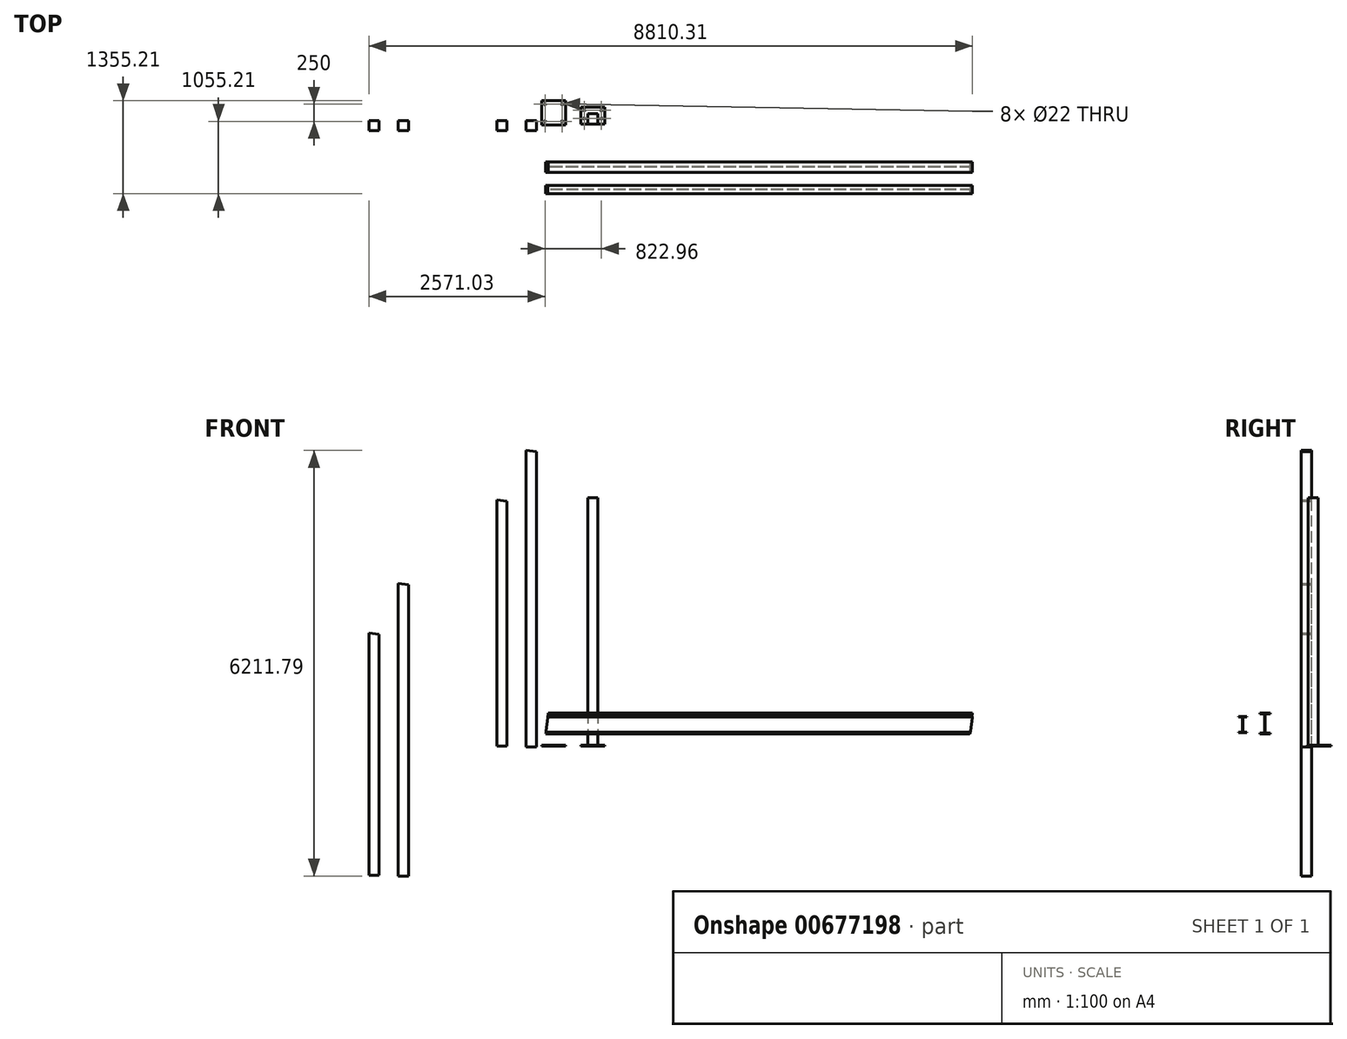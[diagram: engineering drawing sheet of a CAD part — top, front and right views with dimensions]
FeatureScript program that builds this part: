
annotation { "Feature Type Name" : "Feature", "Feature Type Description" : "" }
export const myFeature = defineFeature(function(context is Context, id is Id, definition is map)
    precondition{}
    {
        {
            var Q0;
            Q0=qCreatedBy(makeId("Top.planeOp"),FACE);
            var sketch = newSketch(context, id + "F0", { "sketchPlane" : qUnion([Q0])});
            skLineSegment(sketch, "E0.bottom", {"start": v(-62.2, -61.8) * mm, "end": v(287.8, -61.8) * mm});
            skLineSegment(sketch, "E0.top", {"start": v(-62.2, 288.2) * mm, "end": v(287.8, 288.2) * mm});
            skLineSegment(sketch, "E0.left", {"start": v(-62.2, -61.8) * mm, "end": v(-62.2, 288.2) * mm});
            skLineSegment(sketch, "E0.right", {"start": v(287.8, -61.8) * mm, "end": v(287.8, 288.2) * mm});
            skCircle(sketch, "E1", {"center": v(-12.2, -11.8) * mm, "radius": 11 * mm});
            skCircle(sketch, "E2", {"center": v(-12.2, 238.2) * mm, "radius": 11 * mm});
            skCircle(sketch, "E3", {"center": v(237.8, 238.2) * mm, "radius": 11 * mm});
            skCircle(sketch, "E4", {"center": v(237.8, -11.8) * mm, "radius": 11 * mm});
            skLineSegment(sketch, "E5.bottom", {"start": v(510.77, -51.32) * mm, "end": v(860.77, -51.32) * mm});
            skLineSegment(sketch, "E5.top", {"start": v(510.77, 198.68) * mm, "end": v(860.77, 198.68) * mm});
            skLineSegment(sketch, "E5.left", {"start": v(510.77, -51.32) * mm, "end": v(510.77, 198.68) * mm});
            skLineSegment(sketch, "E5.right", {"start": v(860.77, -51.32) * mm, "end": v(860.77, 198.68) * mm});
            skCircle(sketch, "E6", {"center": v(560.77, 148.68) * mm, "radius": 11 * mm});
            skCircle(sketch, "E7", {"center": v(560.77, 28.68) * mm, "radius": 11 * mm});
            skCircle(sketch, "E8", {"center": v(810.77, 148.68) * mm, "radius": 11 * mm});
            skCircle(sketch, "E9", {"center": v(810.77, 28.68) * mm, "radius": 11 * mm});
            skSolve(sketch);
        }
        {
            var Q0;
            Q0=makeQuery(id+"F0.imprint","IMPRINT",FACE,{"disambiguationData":[TD([[makeQuery(id+"F0.imprint","IMPRINT",EDGE,{"derivedFrom":sQuery(id+"F0.wireOp",EDGE,"E0.bottom")}),1.0]])]});
            var Q1;
            Q1=makeQuery(id+"F0.imprint","IMPRINT",FACE,{"disambiguationData":[TD([[makeQuery(id+"F0.imprint","IMPRINT",EDGE,{"derivedFrom":sQuery(id+"F0.wireOp",EDGE,"E5.bottom")}),1.0]])]});
            extrude(context, id + "F1", {"entities" : qUnion([Q0, Q1]), "depth" : 12 * mm, "offsetDistance" : 25 * mm});
        }
        {
            var Q0;
            Q0=qCreatedBy(makeId("Front.planeOp"),FACE);
            var sketch = newSketch(context, id + "F2", { "sketchPlane" : qUnion([Q0])});
            skLineSegment(sketch, "E10", {"start": v(-288.06, -13.37) * mm, "end": v(-288.06, 4317.72) * mm});
            skLineSegment(sketch, "E11", {"start": v(-288.06, -13.37) * mm, "end": v(-138.06, -13.37) * mm});
            skLineSegment(sketch, "E12", {"start": v(-138.06, -13.37) * mm, "end": v(-138.06, 4299.3) * mm});
            skLineSegment(sketch, "E13", {"start": v(-138.06, 4299.3) * mm, "end": v(-288.06, 4317.72) * mm});
            skLineSegment(sketch, "E14", {"start": v(-715.76, 0) * mm, "end": v(-715.76, 3594.5) * mm});
            skLineSegment(sketch, "E15", {"start": v(-715.76, 0) * mm, "end": v(-565.76, 0) * mm});
            skLineSegment(sketch, "E16", {"start": v(-565.76, 0) * mm, "end": v(-565.76, 3576.09) * mm});
            skLineSegment(sketch, "E17", {"start": v(-565.76, 3576.09) * mm, "end": v(-715.76, 3594.5) * mm});
            skLineSegment(sketch, "E18", {"start": v(-2155.53, -1954.07) * mm, "end": v(-2155.53, 2377.02) * mm});
            skLineSegment(sketch, "E19", {"start": v(-2155.53, -1954.07) * mm, "end": v(-2005.53, -1954.07) * mm});
            skLineSegment(sketch, "E20", {"start": v(-2005.53, -1954.07) * mm, "end": v(-2005.53, 2358.6) * mm});
            skLineSegment(sketch, "E21", {"start": v(-2005.53, 2358.6) * mm, "end": v(-2155.53, 2377.02) * mm});
            skLineSegment(sketch, "E22", {"start": v(-2583.23, -1940.7) * mm, "end": v(-2583.23, 1653.8) * mm});
            skLineSegment(sketch, "E23", {"start": v(-2583.23, -1940.7) * mm, "end": v(-2433.23, -1940.7) * mm});
            skLineSegment(sketch, "E24", {"start": v(-2433.23, -1940.7) * mm, "end": v(-2433.23, 1635.4) * mm});
            skLineSegment(sketch, "E25", {"start": v(-2433.23, 1635.4) * mm, "end": v(-2583.23, 1653.8) * mm});
            skLineSegment(sketch, "E26.0", {"start": v(-2583.23, -1880.7) * mm, "end": v(-2433.23, -1880.7) * mm});
            skLineSegment(sketch, "E27.0", {"start": v(-2155.53, -1894.07) * mm, "end": v(-2005.53, -1894.07) * mm});
            skSolve(sketch);
        }
        {
            var Q0;
            Q0=makeQuery(id+"F2.imprint","IMPRINT",FACE,{"disambiguationData":[TD([[makeQuery(id+"F2.imprint","IMPRINT",EDGE,{"derivedFrom":sQuery(id+"F2.wireOp",EDGE,"E14")}),-1.0]])]});
            var Q1;
            Q1=makeQuery(id+"F2.imprint","IMPRINT",FACE,{"disambiguationData":[TD([[makeQuery(id+"F2.imprint","IMPRINT",EDGE,{"derivedFrom":sQuery(id+"F2.wireOp",EDGE,"E10")}),-1.0]])]});
            var Q2;
            {var subQ0=sQuery(id+"F2.wireOp",EDGE,"E21");Q2=makeQuery(id+"F2.imprint","IMPRINT",FACE,{"disambiguationData":[TD([[makeQuery(id+"F2.imprint","IMPRINT",EDGE,{"derivedFrom":subQ0}),1.0]])]});}
            var Q3;
            {var subQ0=sQuery(id+"F2.wireOp",EDGE,"E25");Q3=makeQuery(id+"F2.imprint","IMPRINT",FACE,{"disambiguationData":[TD([[makeQuery(id+"F2.imprint","IMPRINT",EDGE,{"derivedFrom":subQ0}),1.0]])]});}
            extrude(context, id + "F3", {"entities" : qUnion([Q0, Q1, Q2, Q3]), "depth" : 150 * mm, "offsetDistance" : 25 * mm});
        }
        {
            var Q0;
            Q0=qCreatedBy(makeId("Right.planeOp"),FACE);
            var sketch = newSketch(context, id + "F4", { "sketchPlane" : qUnion([Q0])});
            skLineSegment(sketch, "E28.bottom", {"start": v(-1067, 197.07) * mm, "end": v(-947, 197.07) * mm});
            skLineSegment(sketch, "E28.top", {"start": v(-1067, 437.07) * mm, "end": v(-947, 437.07) * mm});
            skLineSegment(sketch, "E28.left", {"start": v(-1067, 197.07) * mm, "end": v(-1067, 206.87) * mm});
            skLineSegment(sketch, "E28.right", {"start": v(-947, 197.07) * mm, "end": v(-947, 206.87) * mm});
            skLineSegment(sketch, "E29.0", {"start": v(-1067, 427.27) * mm, "end": v(-1010.1, 427.27) * mm});
            skLineSegment(sketch, "E30.0", {"start": v(-1003.9, 206.87) * mm, "end": v(-1003.9, 427.27) * mm});
            skLineSegment(sketch, "E31.0", {"start": v(-1010.1, 211.87) * mm, "end": v(-1010.1, 427.27) * mm});
            skPoint(sketch, "E32.newPointB", {"position": v(-947, 206.87) * mm});
            skLineSegment(sketch, "E33", {"start": v(-1003.9, 206.87) * mm, "end": v(-947, 206.87) * mm});
            skLineSegment(sketch, "E34.left", {"start": v(-1010.1, 211.87) * mm, "end": v(-1010.1, 206.87) * mm});
            skLineSegment(sketch, "E34.right", {"start": v(-1003.9, 211.87) * mm, "end": v(-1003.9, 206.87) * mm});
            skLineSegment(sketch, "E35", {"start": v(-1010.1, 206.87) * mm, "end": v(-1067, 206.87) * mm});
            skLineSegment(sketch, "E36.trimOffspring", {"start": v(-1067, 427.27) * mm, "end": v(-1067, 437.07) * mm});
            skLineSegment(sketch, "E37.trimOffspring", {"start": v(-947, 427.27) * mm, "end": v(-947, 437.07) * mm});
            skLineSegment(sketch, "E38.trimOffspring", {"start": v(-1003.9, 427.27) * mm, "end": v(-947, 427.27) * mm});
            skLineSegment(sketch, "E39.bottom", {"start": v(-754.62, 182.23) * mm, "end": v(-604.62, 182.23) * mm});
            skLineSegment(sketch, "E39.top", {"start": v(-754.62, 482.23) * mm, "end": v(-604.62, 482.23) * mm});
            skLineSegment(sketch, "E39.left", {"start": v(-754.62, 182.23) * mm, "end": v(-754.62, 192.93) * mm});
            skLineSegment(sketch, "E39.right", {"start": v(-604.62, 182.23) * mm, "end": v(-604.62, 192.93) * mm});
            skLineSegment(sketch, "E40.bottom", {"start": v(-679.62, 182.23) * mm, "end": v(-679.62, 182.23) * mm});
            skLineSegment(sketch, "E40.top", {"start": v(-679.62, 482.23) * mm, "end": v(-679.62, 482.23) * mm});
            skLineSegment(sketch, "E41.0", {"start": v(-754.62, 192.93) * mm, "end": v(-683.17, 192.93) * mm});
            skLineSegment(sketch, "E42.0", {"start": v(-676.07, 192.93) * mm, "end": v(-676.07, 471.53) * mm});
            skLineSegment(sketch, "E43.0", {"start": v(-683.17, 192.93) * mm, "end": v(-683.17, 471.53) * mm});
            skLineSegment(sketch, "E44.trimOffspring", {"start": v(-754.62, 471.53) * mm, "end": v(-754.62, 482.23) * mm});
            skLineSegment(sketch, "E45.trimOffspring", {"start": v(-604.62, 471.53) * mm, "end": v(-604.62, 482.23) * mm});
            skLineSegment(sketch, "E46.trimOffspring", {"start": v(-676.07, 192.93) * mm, "end": v(-604.62, 192.93) * mm});
            skLineSegment(sketch, "E47.trimOffspring", {"start": v(-676.07, 471.53) * mm, "end": v(-604.62, 471.53) * mm});
            skLineSegment(sketch, "E48", {"start": v(-754.62, 471.53) * mm, "end": v(-683.17, 471.53) * mm});
            skSolve(sketch);
        }
        {
            var Q0;
            Q0=makeQuery(id+"F4.imprint","IMPRINT",FACE,{"disambiguationData":[TD([[makeQuery(id+"F4.imprint","IMPRINT",EDGE,{"derivedFrom":sQuery(id+"F4.wireOp",EDGE,"E28.bottom")}),1.0]])]});
            var Q1;
            Q1=makeQuery(id+"F4.imprint","IMPRINT",FACE,{"disambiguationData":[TD([[makeQuery(id+"F4.imprint","IMPRINT",EDGE,{"derivedFrom":sQuery(id+"F4.wireOp",EDGE,"E39.bottom")}),1.0]])]});
            extrude(context, id + "F5", {"entities" : qUnion([Q0, Q1]), "depth" : 6227.08 * mm, "offsetDistance" : 25 * mm});
        }
        {
            var Q0;
            Q0=makeQuery(id+"F5.opExtrude","SWEPT_FACE",FACE,{"disambiguationData":[OSD([sQuery(id+"F4.wireOp",EDGE,"E28.left")])]});
            var sketch = newSketch(context, id + "F6", { "sketchPlane" : qUnion([Q0])});
            skLineSegment(sketch, "E49", {"start": v(0, 197.07) * mm, "end": v(0, 437.07) * mm});
            skLineSegment(sketch, "E50", {"start": v(0, 437.07) * mm, "end": v(30.91, 437.07) * mm});
            skLineSegment(sketch, "E51", {"start": v(0, 197.07) * mm, "end": v(30.91, 437.07) * mm});
            skLineSegment(sketch, "E52", {"start": v(6227.08, 197.07) * mm, "end": v(6196.17, 197.07) * mm});
            skLineSegment(sketch, "E53", {"start": v(6227.08, 197.07) * mm, "end": v(6227.08, 437.07) * mm});
            skLineSegment(sketch, "E54", {"start": v(6227.08, 437.07) * mm, "end": v(6196.17, 197.07) * mm});
            skSolve(sketch);
        }
        {
            var Q0;
            Q0 = qSketchRegion(id + "F6", true);
            extrude(context, id + "F7", {"entities" : qUnion([Q0]), "operationType" : NewBodyOperationType.REMOVE, "oppositeDirection" : true, "depth" : 120 * mm, "offsetDistance" : 25 * mm});
        }
        {
            var Q0;
            Q0=makeQuery(id+"F5.opExtrude","SWEPT_EDGE",EDGE,{"disambiguationData":[OSD([sQuery(id+"F4.wireOp",EDGE,"E34.left"),sQuery(id+"F4.wireOp",EDGE,"E35")])]});
            var Q1;
            Q1=makeQuery(id+"F5.opExtrude","SWEPT_EDGE",EDGE,{"disambiguationData":[OSD([sQuery(id+"F4.wireOp",EDGE,"E29.0"),sQuery(id+"F4.wireOp",EDGE,"E31.0")])]});
            var Q2;
            Q2=makeQuery(id+"F5.opExtrude","SWEPT_EDGE",EDGE,{"disambiguationData":[OSD([sQuery(id+"F4.wireOp",EDGE,"E30.0"),sQuery(id+"F4.wireOp",EDGE,"E33")])]});
            var Q3;
            Q3=makeQuery(id+"F5.opExtrude","SWEPT_EDGE",EDGE,{"disambiguationData":[OSD([sQuery(id+"F4.wireOp",EDGE,"E30.0"),sQuery(id+"F4.wireOp",EDGE,"E38.trimOffspring")])]});
            fillet(context, id + "F8", {"entities" : qUnion([Q0, Q1, Q2, Q3]), "radius" : 15 * mm, "tangentPropagation" : true, "allowEdgeOverflow" : false});
        }
        {
            var Q0;
            Q0=makeQuery(id+"F1.opExtrude","CAP_FACE",FACE,{"disambiguationData":[OSD([sQuery(id+"F0.wireOp",EDGE,"E5.bottom"),sQuery(id+"F0.wireOp",EDGE,"E5.top"),sQuery(id+"F0.wireOp",EDGE,"E5.left"),sQuery(id+"F0.wireOp",EDGE,"E5.right"),sQuery(id+"F0.wireOp",EDGE,"E6"),sQuery(id+"F0.wireOp",EDGE,"E7"),sQuery(id+"F0.wireOp",EDGE,"E8"),sQuery(id+"F0.wireOp",EDGE,"E9")])],"isStart":false});
            var sketch = newSketch(context, id + "F9", { "sketchPlane" : qUnion([Q0])});
            skLineSegment(sketch, "E55", {"start": v(685.77, 198.68) * mm, "end": v(685.77, 23.68) * mm});
            skPoint(sketch, "E56", {"position": v(685.77, 23.68) * mm});
            skLineSegment(sketch, "E57.bottom", {"start": v(760.77, 98.68) * mm, "end": v(610.77, 98.68) * mm});
            skLineSegment(sketch, "E57.top", {"start": v(760.77, -51.32) * mm, "end": v(610.77, -51.32) * mm});
            skLineSegment(sketch, "E57.left", {"start": v(760.77, 98.68) * mm, "end": v(760.77, -51.32) * mm});
            skLineSegment(sketch, "E57.right", {"start": v(610.77, 98.68) * mm, "end": v(610.77, -51.32) * mm});
            skSolve(sketch);
        }
        {
            var Q0;
            Q0=makeQuery(id+"F9.imprint","IMPRINT",FACE,{"disambiguationData":[TD([[makeQuery(id+"F9.imprint","IMPRINT",EDGE,{"derivedFrom":sQuery(id+"F9.wireOp",EDGE,"E57.top")}),1.0]])]});
            extrude(context, id + "F10", {"entities" : qUnion([Q0]), "depth" : 3616 * mm, "offsetDistance" : 25 * mm});
        }
        {
            var Q0;
            Q0=makeQuery(id+"F5.opExtrude","SWEPT_FACE",FACE,{"disambiguationData":[OSD([sQuery(id+"F4.wireOp",EDGE,"E45.trimOffspring")])]});
            var sketch = newSketch(context, id + "F11", { "sketchPlane" : qUnion([Q0])});
            skLineSegment(sketch, "E58", {"start": v(0, 182.2) * mm, "end": v(0, 482.23) * mm});
            skLineSegment(sketch, "E59", {"start": v(0, 482.23) * mm, "end": v(-36.83, 482.23) * mm});
            skLineSegment(sketch, "E60", {"start": v(-36.83, 482.23) * mm, "end": v(0, 182.2) * mm});
            skLineSegment(sketch, "E61", {"start": v(-6227.08, 482.23) * mm, "end": v(-6227.08, 182.2) * mm});
            skLineSegment(sketch, "E62", {"start": v(-6227.08, 182.2) * mm, "end": v(-6190.26, 182.2) * mm});
            skLineSegment(sketch, "E63", {"start": v(-6190.26, 182.2) * mm, "end": v(-6227.08, 482.23) * mm});
            skSolve(sketch);
        }
        {
            var Q0;
            {var subQ3=sQuery(id+"F11.wireOp",EDGE,"E62");Q0=makeQuery(id+"F11.imprint","IMPRINT",FACE,{"disambiguationData":[TD([[makeQuery(id+"F11.imprint","IMPRINT",EDGE,{"derivedFrom":subQ3}),1.0]])]});}
            var Q1;
            {var subQ0=sQuery(id+"F11.wireOp",EDGE,"E58");var subQ3=sQuery(id+"F11.wireOp",EDGE,"E60");var subQ4=makeQuery(id+"F11.imprint","INTERSECT",VERTEX,{"derivedFrom":[subQ0,subQ3]});Q1=makeQuery(id+"F11.imprint","IMPRINT",FACE,{"disambiguationData":[TD([[makeQuery(id+"F11.imprint","IMPRINT",EDGE,{"disambiguationData":[TD([[subQ4,-1.0]])],"derivedFrom":subQ0}),1.0]])]});}
            var Q2;
            {var subQ0=sQuery(id+"F11.wireOp",EDGE,"E59");Q2=makeQuery(id+"F11.imprint","IMPRINT",FACE,{"disambiguationData":[TD([[makeQuery(id+"F11.imprint","IMPRINT",EDGE,{"derivedFrom":subQ0}),-1.0]])]});}
            extrude(context, id + "F12", {"entities" : qUnion([Q0, Q1, Q2]), "operationType" : NewBodyOperationType.REMOVE, "oppositeDirection" : true, "depth" : 150 * mm, "offsetDistance" : 25 * mm});
        }
    });
